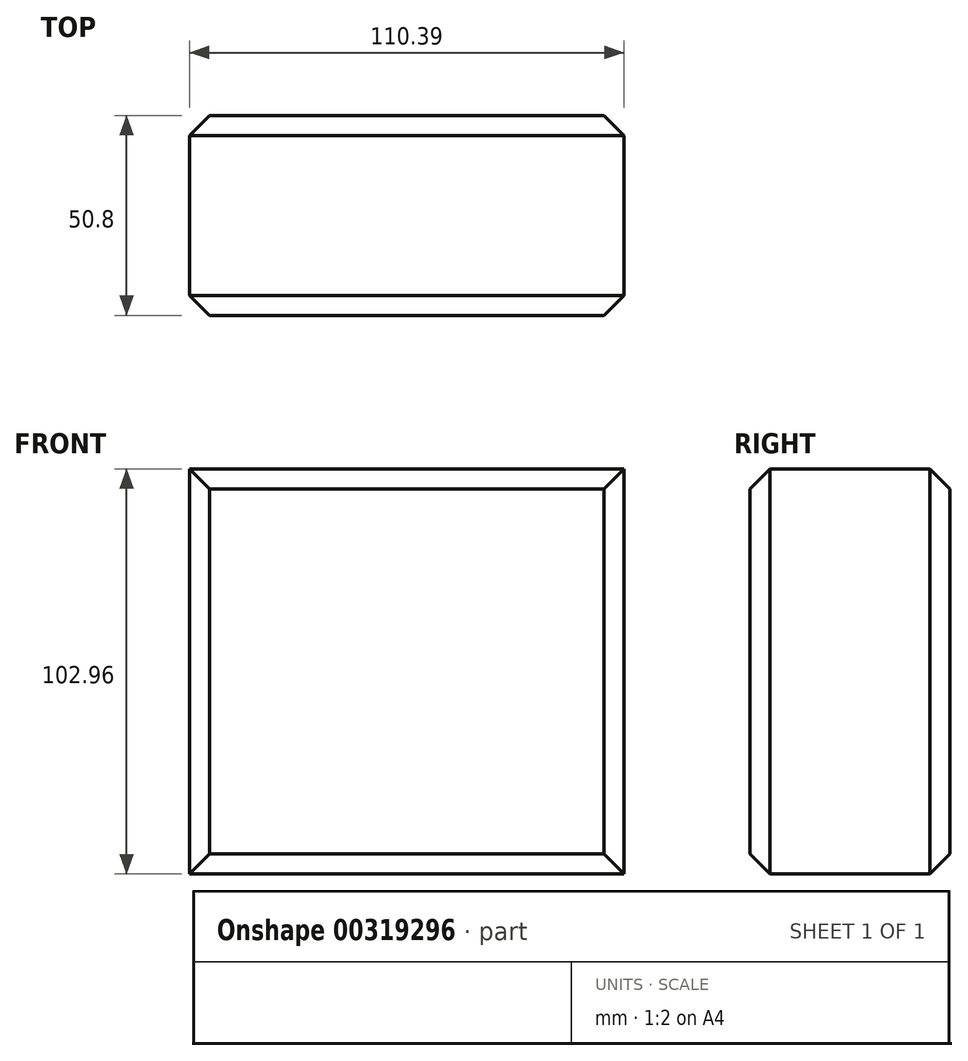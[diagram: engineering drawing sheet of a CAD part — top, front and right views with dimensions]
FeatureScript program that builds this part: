
annotation { "Feature Type Name" : "Feature", "Feature Type Description" : "" }
export const myFeature = defineFeature(function(context is Context, id is Id, definition is map)
    precondition{}
    {
        {
            var Q0;
            Q0=qCreatedBy(makeId("Front.planeOp"),FACE);
            var sketch = newSketch(context, id + "F0", { "sketchPlane" : qUnion([Q0])});
            skLineSegment(sketch, "E0.bottom", {"start": v(-47.2, 49.45) * mm, "end": v(63.2, 49.45) * mm});
            skLineSegment(sketch, "E0.top", {"start": v(-47.2, -53.51) * mm, "end": v(63.2, -53.51) * mm});
            skLineSegment(sketch, "E0.left", {"start": v(-47.2, 49.45) * mm, "end": v(-47.2, -53.51) * mm});
            skLineSegment(sketch, "E0.right", {"start": v(63.2, 49.45) * mm, "end": v(63.2, -53.51) * mm});
            skSolve(sketch);
        }
        {
            var Q0;
            Q0=makeQuery(id+"F0.imprint","IMPRINT",FACE,{"disambiguationData":[TD([[makeQuery(id+"F0.imprint","IMPRINT",EDGE,{"derivedFrom":sQuery(id+"F0.wireOp",EDGE,"E0.bottom")}),-1.0]])]});
            extrude(context, id + "F1", {"entities" : qUnion([Q0]), "depth" : 50.8 * mm});
        }
        {
            var Q0;
            Q0=makeQuery(id+"F1.opExtrude","CAP_FACE",FACE,{"disambiguationData":[OSD([sQuery(id+"F0.wireOp",EDGE,"E0.bottom"),sQuery(id+"F0.wireOp",EDGE,"E0.top"),sQuery(id+"F0.wireOp",EDGE,"E0.left"),sQuery(id+"F0.wireOp",EDGE,"E0.right")])],"isStart":false});
            chamfer(context, id + "F2", {"entities" : qUnion([Q0]), "width" : 5.08 * mm, "tangentPropagation" : true});
        }
        {
            var Q0;
            Q0=makeQuery(id+"F1.opExtrude","CAP_FACE",FACE,{"disambiguationData":[OSD([sQuery(id+"F0.wireOp",EDGE,"E0.bottom"),sQuery(id+"F0.wireOp",EDGE,"E0.top"),sQuery(id+"F0.wireOp",EDGE,"E0.left"),sQuery(id+"F0.wireOp",EDGE,"E0.right")])],"isStart":true});
            chamfer(context, id + "F3", {"entities" : qUnion([Q0]), "chamferType" : ChamferType.TWO_OFFSETS, "width1" : 5.08 * mm, "oppositeDirection" : false, "width2" : 5.08 * mm, "tangentPropagation" : true});
        }
    });
